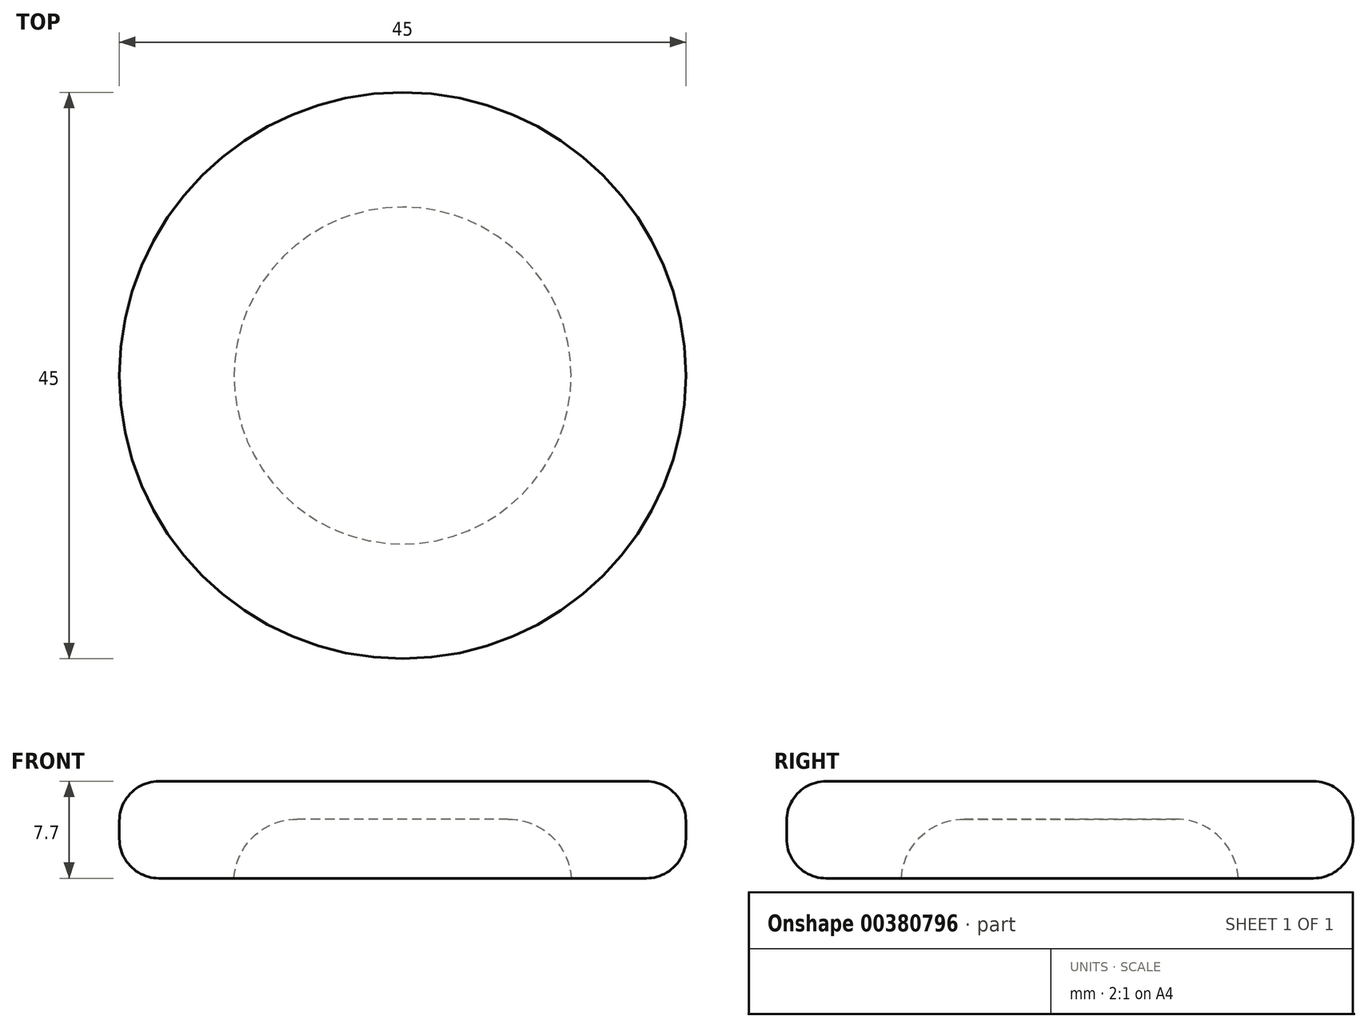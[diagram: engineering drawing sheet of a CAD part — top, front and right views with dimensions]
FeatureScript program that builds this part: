
annotation { "Feature Type Name" : "Feature", "Feature Type Description" : "" }
export const myFeature = defineFeature(function(context is Context, id is Id, definition is map)
    precondition{}
    {
        {
            var Q0;
            Q0=qCreatedBy(makeId("Top.planeOp"),FACE);
            var sketch = newSketch(context, id + "F0", { "sketchPlane" : qUnion([Q0])});
            skCircle(sketch, "E0", {"center": v(-30.77, 10.9) * mm, "radius": 22.5 * mm});
            skCircle(sketch, "E1", {"center": v(-30.77, 10.9) * mm, "radius": 13.39 * mm});
            skSolve(sketch);
        }
        {
            var Q0;
            Q0 = qSketchRegion(id + "F0", true);
            extrude(context, id + "F1", {"entities" : qUnion([Q0]), "oppositeDirection" : true, "depth" : 7.7 * mm});
        }
        {
            var Q0;
            Q0=makeQuery(id+"F1.opExtrude","SWEPT_FACE",FACE,{"disambiguationData":[OSD([sQuery(id+"F0.wireOp",EDGE,"E0")])]});
            fillet(context, id + "F2", {"entities" : qUnion([Q0]), "radius" : 3.14 * mm, "tangentPropagation" : true, "allowEdgeOverflow" : false});
        }
        {
            var Q0;
            Q0=makeQuery(id+"F0.imprint","IMPRINT",FACE,{"disambiguationData":[TD([[makeQuery(id+"F0.imprint","IMPRINT",EDGE,{"derivedFrom":sQuery(id+"F0.wireOp",EDGE,"E1")}),1.0]])]});
            extrude(context, id + "F3", {"entities" : qUnion([Q0]), "operationType" : NewBodyOperationType.ADD, "oppositeDirection" : true, "depth" : 3 * mm});
        }
        {
            var Q0;
            Q0=makeQuery(id+"F3.opExtrude","CAP_FACE",FACE,{"disambiguationData":[OSD([sQuery(id+"F0.wireOp",EDGE,"E1")])],"isStart":false});
            fillet(context, id + "F4", {"entities" : qUnion([Q0]), "radius" : 5 * mm, "tangentPropagation" : true, "allowEdgeOverflow" : false});
        }
    });
